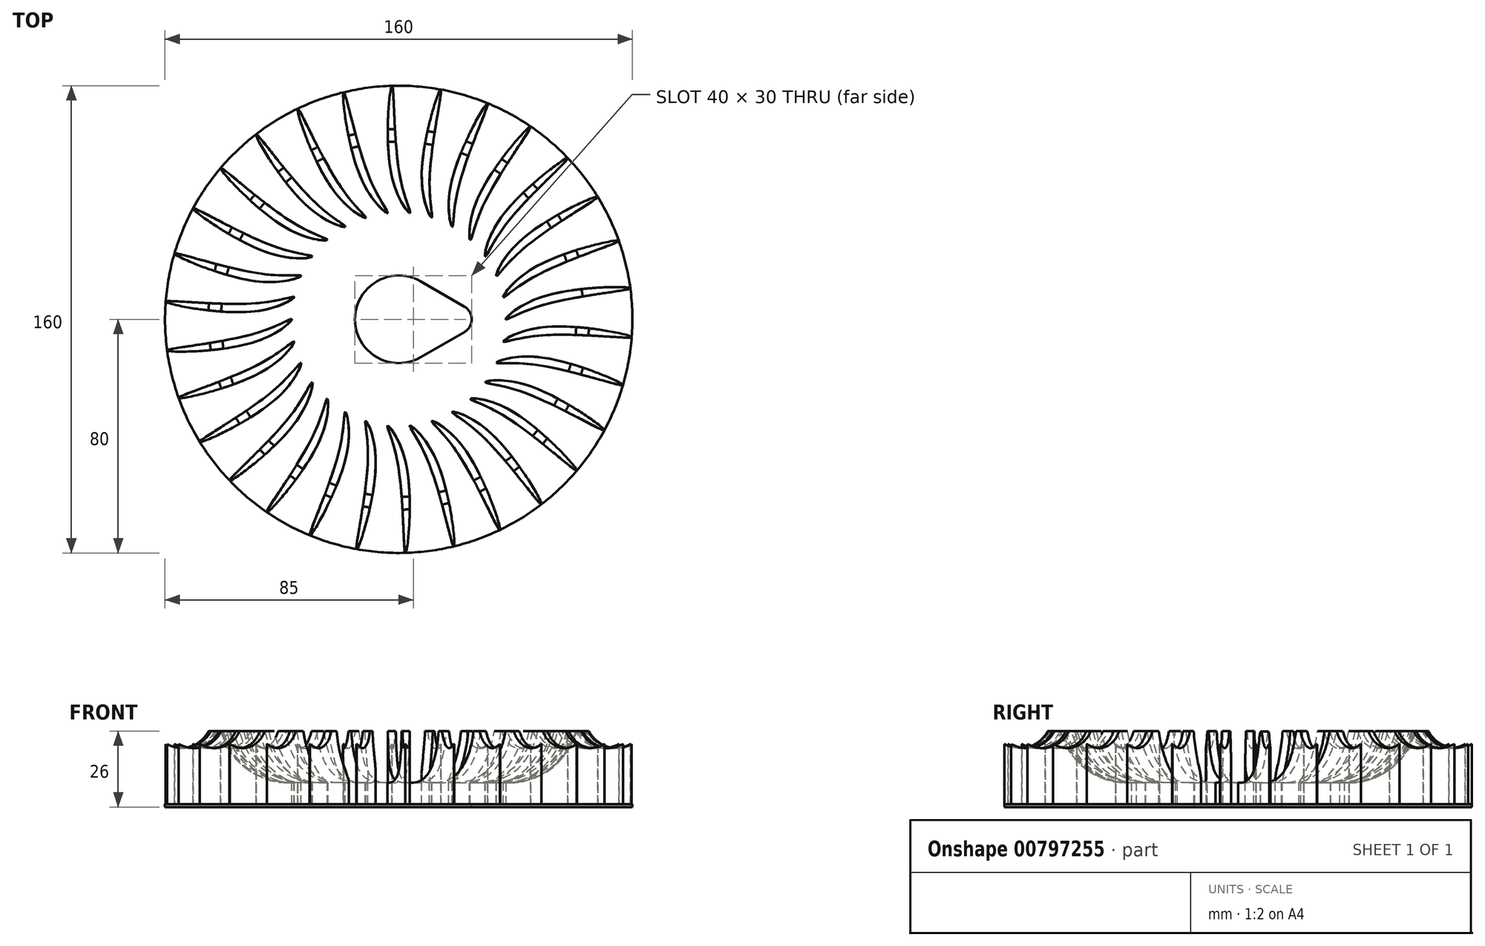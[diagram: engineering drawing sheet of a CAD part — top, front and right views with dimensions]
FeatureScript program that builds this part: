
annotation { "Feature Type Name" : "Feature", "Feature Type Description" : "" }
export const myFeature = defineFeature(function(context is Context, id is Id, definition is map)
    precondition{}
    {
        {
            var Q0;
            Q0=qCreatedBy(makeId("Top.planeOp"),FACE);
            var sketch = newSketch(context, id + "F0", { "sketchPlane" : qUnion([Q0])});
            skCircle(sketch, "E0", {"center": v(0, 0) * mm, "radius": 80 * mm});
            skSolve(sketch);
        }
        {
            var Q0;
            Q0 = qSketchRegion(id + "F0", true);
            extrude(context, id + "F1", {"entities" : qUnion([Q0]), "depth" : 1 * mm, "offsetDistance" : 25 * mm});
        }
        {
            var Q0;
            Q0=makeQuery(id+"F1.opExtrude","CAP_FACE",FACE,{"disambiguationData":[OSD([sQuery(id+"F0.wireOp",EDGE,"E0")])],"isStart":false});
            var sketch = newSketch(context, id + "F2", { "sketchPlane" : qUnion([Q0])});
            skFitSpline(sketch, "E1", {"points": [v(36.6, 0) * mm, v(48.83, 7.6) * mm, v(79.29, 10.64) * mm, v(48.83, 4.74) * mm, v(36.6, 0) * mm]});
            skSolve(sketch);
        }
        {
            var Q0;
            Q0 = qSketchRegion(id + "F2", true);
            extrude(context, id + "F3", {"entities" : qUnion([Q0]), "operationType" : NewBodyOperationType.ADD, "depth" : 25 * mm, "offsetDistance" : 25 * mm});
        }
        {
            var Q0;
            Q0=makeQuery(id+"F1.opExtrude","SWEPT_BODY",BODY,{"disambiguationData":[OSD([sQuery(id+"F0.wireOp",EDGE,"E0")])]});
            var Q1;
            Q1=makeQuery(id+"F1.opExtrude","CAP_EDGE",EDGE,{"disambiguationData":[OSD([sQuery(id+"F0.wireOp",EDGE,"E0")])],"isStart":true});
            circularPattern(context, id + "F4", {"operationType" : NewBodyOperationType.ADD, "entities" : qUnion([Q0]), "axis" : qUnion([Q1]), "angle" : 360 * degree, "instanceCount" : 30, "equalSpace" : true});
        }
        {
            var Q0;
            Q0=qCreatedBy(makeId("Front.planeOp"),FACE);
            var sketch = newSketch(context, id + "F5", { "sketchPlane" : qUnion([Q0])});
            skCircle(sketch, "E2", {"center": v(37.9, 31.96) * mm, "radius": 23.68 * mm});
            skCircle(sketch, "E3", {"center": v(74.74, 30.93) * mm, "radius": 10.76 * mm});
            skSolve(sketch);
        }
        {
            var Q0;
            Q0 = qSketchRegion(id + "F5", true);
            var Q1;
            Q1=makeQuery(id+"F1.opExtrude","SWEPT_FACE",FACE,{"disambiguationData":[OSD([sQuery(id+"F0.wireOp",EDGE,"E0")])]});
            revolve(context, id + "F6", {"operationType" : NewBodyOperationType.REMOVE, "surfaceOperationType" : NewSurfaceOperationType.NEW, "entities" : qUnion([Q0]), "axis" : qUnion([Q1]), "revolveType" : RevolveType.FULL});
        }
        {
            var Q0;
            Q0=makeQuery(id+"F6.boolean.opBoolean","INTERSECT",EDGE,{"derivedFrom":[makeQuery(id+"F3.opExtrude","CAP_FACE",FACE,{"disambiguationData":[OSD([sQuery(id+"F2.wireOp",EDGE,"E1")])],"isStart":false}),makeQuery(id+"F6.opRevolve","SWEPT_FACE",FACE,{"disambiguationData":[OSD([sQuery(id+"F5.wireOp",EDGE,"E2")])]})]});
            var Q1;
            Q1=makeQuery(id+"F6.boolean.opBoolean","INTERSECT",EDGE,{"derivedFrom":[makeQuery(id+"F3.opExtrude","CAP_FACE",FACE,{"disambiguationData":[OSD([sQuery(id+"F2.wireOp",EDGE,"E1")])],"isStart":false}),makeQuery(id+"F6.opRevolve","SWEPT_FACE",FACE,{"disambiguationData":[OSD([sQuery(id+"F5.wireOp",EDGE,"E3")])]})]});
            fillet(context, id + "F7", {"entities" : qUnion([Q0, Q1]), "radius" : 5 * mm, "tangentPropagation" : true, "allowEdgeOverflow" : false});
        }
        {
            var Q0;
            Q0=makeQuery(id+"F1.opExtrude","CAP_FACE",FACE,{"disambiguationData":[OSD([sQuery(id+"F0.wireOp",EDGE,"E0")])],"isStart":false});
            var sketch = newSketch(context, id + "F8", { "sketchPlane" : qUnion([Q0])});
            skArc(sketch, "E4", {"start": v(7.5, 13) * mm, "mid": v(-15, 0) * mm, "end": v(7.5, -13) * mm});
            skArc(sketch, "E5", {"start": v(22.5, -4.33) * mm, "mid": v(25, 0) * mm, "end": v(22.5, 4.33) * mm});
            skLineSegment(sketch, "E6", {"start": v(7.5, -13) * mm, "end": v(22.5, -4.33) * mm});
            skLineSegment(sketch, "E7", {"start": v(22.5, 4.33) * mm, "end": v(7.5, 13) * mm});
            skSolve(sketch);
        }
        {
            var Q0;
            Q0 = qSketchRegion(id + "F8", true);
            extrude(context, id + "F9", {"entities" : qUnion([Q0]), "operationType" : NewBodyOperationType.REMOVE, "endBound" : BoundingType.UP_TO_NEXT, "oppositeDirection" : true, "depth" : 25 * mm, "offsetDistance" : 25 * mm});
        }
    });
